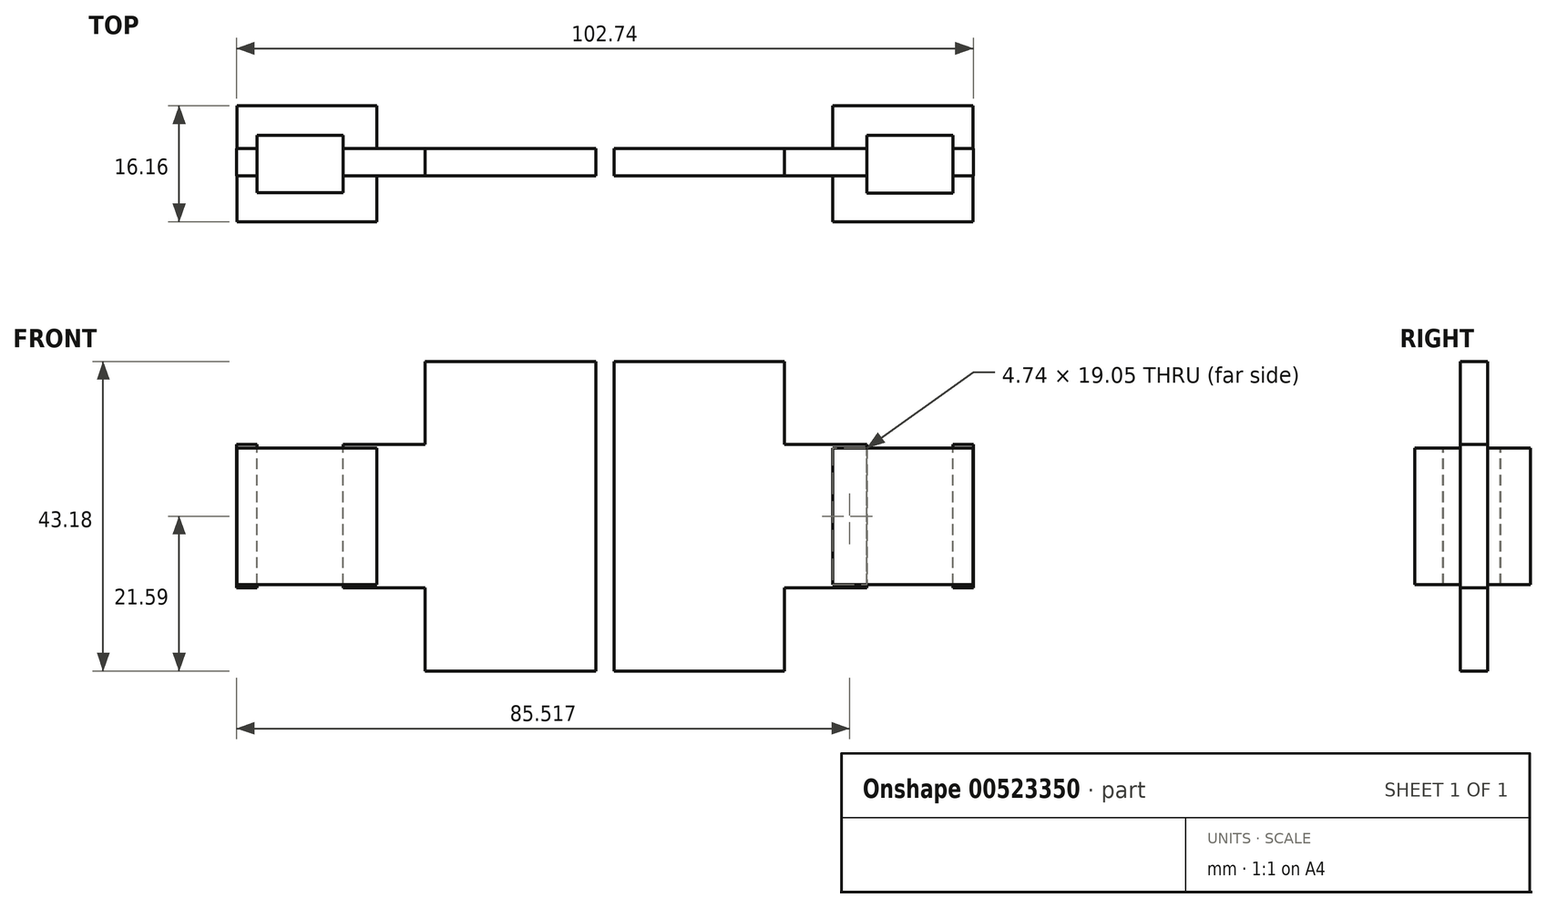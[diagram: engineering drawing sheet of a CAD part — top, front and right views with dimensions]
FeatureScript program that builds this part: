
annotation { "Feature Type Name" : "Feature", "Feature Type Description" : "" }
export const myFeature = defineFeature(function(context is Context, id is Id, definition is map)
    precondition{}
    {
        {
            var Q0;
            Q0=qCreatedBy(makeId("Front.planeOp"),FACE);
            var sketch = newSketch(context, id + "F0", { "sketchPlane" : qUnion([Q0])});
            skLineSegment(sketch, "E0.bottom", {"start": v(-25.05, 21.6) * mm, "end": v(25.05, 21.6) * mm});
            skLineSegment(sketch, "E0.top", {"start": v(-25.05, -21.6) * mm, "end": v(25.05, -21.6) * mm});
            skLineSegment(sketch, "E0.left", {"start": v(-25.05, 21.6) * mm, "end": v(-25.05, -21.59) * mm});
            skLineSegment(sketch, "E0.right", {"start": v(25.05, 21.6) * mm, "end": v(25.05, -21.59) * mm});
            skSolve(sketch);
        }
        {
            var Q0;
            Q0=qCreatedBy(makeId("Front.planeOp"),FACE);
            var sketch = newSketch(context, id + "F1", { "sketchPlane" : qUnion([Q0])});
            skLineSegment(sketch, "E1.bottom", {"start": v(-51.37, 10) * mm, "end": v(51.37, 10) * mm});
            skLineSegment(sketch, "E1.top", {"start": v(-51.37, -10) * mm, "end": v(51.37, -10) * mm});
            skLineSegment(sketch, "E1.left", {"start": v(-51.37, 10) * mm, "end": v(-51.37, -10) * mm});
            skLineSegment(sketch, "E1.right", {"start": v(51.37, 10) * mm, "end": v(51.37, -10) * mm});
            skSolve(sketch);
        }
        {
            var Q0;
            Q0=makeQuery(id+"F0.imprint","IMPRINT",FACE,{"disambiguationData":[TD([[makeQuery(id+"F0.imprint","IMPRINT",EDGE,{"derivedFrom":sQuery(id+"F0.wireOp",EDGE,"E0.bottom")}),-1.0]])]});
            var Q1;
            Q1 = qSketchRegion(id + "F0", true);
            extrude(context, id + "F2", {"entities" : qUnion([Q0, Q1]), "depth" : 3.8 * mm, "offsetDistance" : 25.4 * mm});
        }
        {
            var Q0;
            Q0 = qSketchRegion(id + "F1", true);
            extrude(context, id + "F3", {"entities" : qUnion([Q0]), "operationType" : NewBodyOperationType.ADD, "depth" : 3.8 * mm, "offsetDistance" : 25.4 * mm});
        }
        {
            var Q0;
            Q0=qCreatedBy(makeId("Top.planeOp"),FACE);
            var sketch = newSketch(context, id + "F4", { "sketchPlane" : qUnion([Q0])});
            skLineSegment(sketch, "E2.bottom", {"start": v(-48.52, -6.11) * mm, "end": v(-36.52, -6.11) * mm});
            skLineSegment(sketch, "E2.top", {"start": v(-48.52, 1.89) * mm, "end": v(-36.52, 1.89) * mm});
            skLineSegment(sketch, "E2.left", {"start": v(-48.52, -6.11) * mm, "end": v(-48.52, 1.89) * mm});
            skLineSegment(sketch, "E2.right", {"start": v(-36.52, -6.11) * mm, "end": v(-36.52, 1.89) * mm});
            skSolve(sketch);
        }
        {
            var Q0;
            Q0=qCreatedBy(makeId("Front.planeOp"),FACE);
            var sketch = newSketch(context, id + "F5", { "sketchPlane" : qUnion([Q0])});
            skLineSegment(sketch, "E3.bottom", {"start": v(-1.27, 21.6) * mm, "end": v(1.27, 21.6) * mm});
            skLineSegment(sketch, "E3.top", {"start": v(-1.27, -21.6) * mm, "end": v(1.27, -21.6) * mm});
            skLineSegment(sketch, "E3.left", {"start": v(-1.27, 21.6) * mm, "end": v(-1.27, -21.6) * mm});
            skLineSegment(sketch, "E3.right", {"start": v(1.27, 21.6) * mm, "end": v(1.27, -21.6) * mm});
            skSolve(sketch);
        }
        {
            var Q0;
            Q0 = qSketchRegion(id + "F5", true);
            extrude(context, id + "F6", {"entities" : qUnion([Q0]), "operationType" : NewBodyOperationType.REMOVE, "depth" : 3.8 * mm, "offsetDistance" : 25.4 * mm});
        }
        {
            var Q0;
            Q0=qCreatedBy(makeId("Top.planeOp"),FACE);
            var sketch = newSketch(context, id + "F7", { "sketchPlane" : qUnion([Q0])});
            skLineSegment(sketch, "E4.bottom", {"start": v(-51.3, -10.17) * mm, "end": v(-31.77, -10.17) * mm});
            skLineSegment(sketch, "E4.top", {"start": v(-51.3, 6) * mm, "end": v(-31.77, 6) * mm});
            skLineSegment(sketch, "E4.left", {"start": v(-51.3, -10.17) * mm, "end": v(-51.3, 6) * mm});
            skLineSegment(sketch, "E4.right", {"start": v(-31.77, -10.17) * mm, "end": v(-31.77, 6) * mm});
            skSolve(sketch);
        }
        {
            var Q0;
            Q0 = qSketchRegion(id + "F7", true);
            extrude(context, id + "F8", {"entities" : qUnion([Q0]), "depth" : 19.05 * mm, "offsetDistance" : 25.4 * mm, "symmetric" : true});
        }
        {
            var Q0;
            Q0 = qSketchRegion(id + "F4", true);
            var Q1;
            Q1=sQuery(id+"F4.wireOp",EDGE,"E2.bottom");
            extrude(context, id + "F9", {"entities" : qUnion([Q0]), "operationType" : NewBodyOperationType.REMOVE, "surfaceEntities" : qUnion([Q1]), "oppositeDirection" : true, "depth" : 50.8 * mm, "offsetDistance" : 25.4 * mm, "symmetric" : true});
        }
        {
            var Q0;
            Q0=makeQuery(id+"F8.opExtrude","SWEPT_BODY",BODY,{"disambiguationData":[OSD([sQuery(id+"F7.wireOp",EDGE,"E4.bottom"),sQuery(id+"F7.wireOp",EDGE,"E4.top"),sQuery(id+"F7.wireOp",EDGE,"E4.left"),sQuery(id+"F7.wireOp",EDGE,"E4.right")])]});
            var Q1;
            Q1=qCreatedBy(makeId("Right.planeOp"),FACE);
            mirror(context, id + "F10", {"operationType" : NewBodyOperationType.ADD, "entities" : qUnion([Q0]), "mirrorPlane" : qUnion([Q1])});
        }
        {
            var Q0;
            Q0=qCreatedBy(makeId("Top.planeOp"),FACE);
            var sketch = newSketch(context, id + "F11", { "sketchPlane" : qUnion([Q0])});
            skLineSegment(sketch, "E5.bottom", {"start": v(36.55, -6.19) * mm, "end": v(48.54, -6.19) * mm});
            skLineSegment(sketch, "E5.top", {"start": v(36.55, 1.77) * mm, "end": v(48.54, 1.77) * mm});
            skLineSegment(sketch, "E5.left", {"start": v(36.55, -6.19) * mm, "end": v(36.55, 1.77) * mm});
            skLineSegment(sketch, "E5.right", {"start": v(48.54, -6.19) * mm, "end": v(48.54, 1.77) * mm});
            skSolve(sketch);
        }
        {
            var Q0;
            Q0 = qSketchRegion(id + "F11", true);
            extrude(context, id + "F12", {"entities" : qUnion([Q0]), "operationType" : NewBodyOperationType.REMOVE, "oppositeDirection" : true, "depth" : 50.8 * mm, "offsetDistance" : 25.4 * mm, "symmetric" : true});
        }
    });
